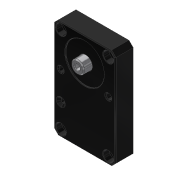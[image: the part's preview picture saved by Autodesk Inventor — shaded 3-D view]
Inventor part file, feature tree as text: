
AUTODESK INVENTOR PART (.ipt)
format: ipt  version: 2019.4 (Build 234330000, 330)  size: 212,480 bytes
history: native  units: mm
features: sketch x4, extrude x3, chamfer x3, other x1, revolve x1
ambient origin geometry x8: Origin, YZ Plane, XZ Plane, XY Plane, X Axis, Y Axis, Z Axis, Center Point
bodies: Body1 (feature_tree)
feature tree (12):
  other  "ソリッド1"
  extrude  "押し出し1"  Depth=2.5mm
  chamfer  "面取り1"  Distance=28.5mm
  extrude  "押し出し2"  Depth=46.5mm
  extrude  "押し出し3"  Depth=8.0mm
  chamfer  "面取り2"  Distance=8.0mm
  chamfer  "面取り3"  Distance=22.0mm
  revolve  "回転1"
  sketch  "スケッチ1"
  sketch  "スケッチ2"
  sketch  "スケッチ3"
  sketch  "スケッチ5"
